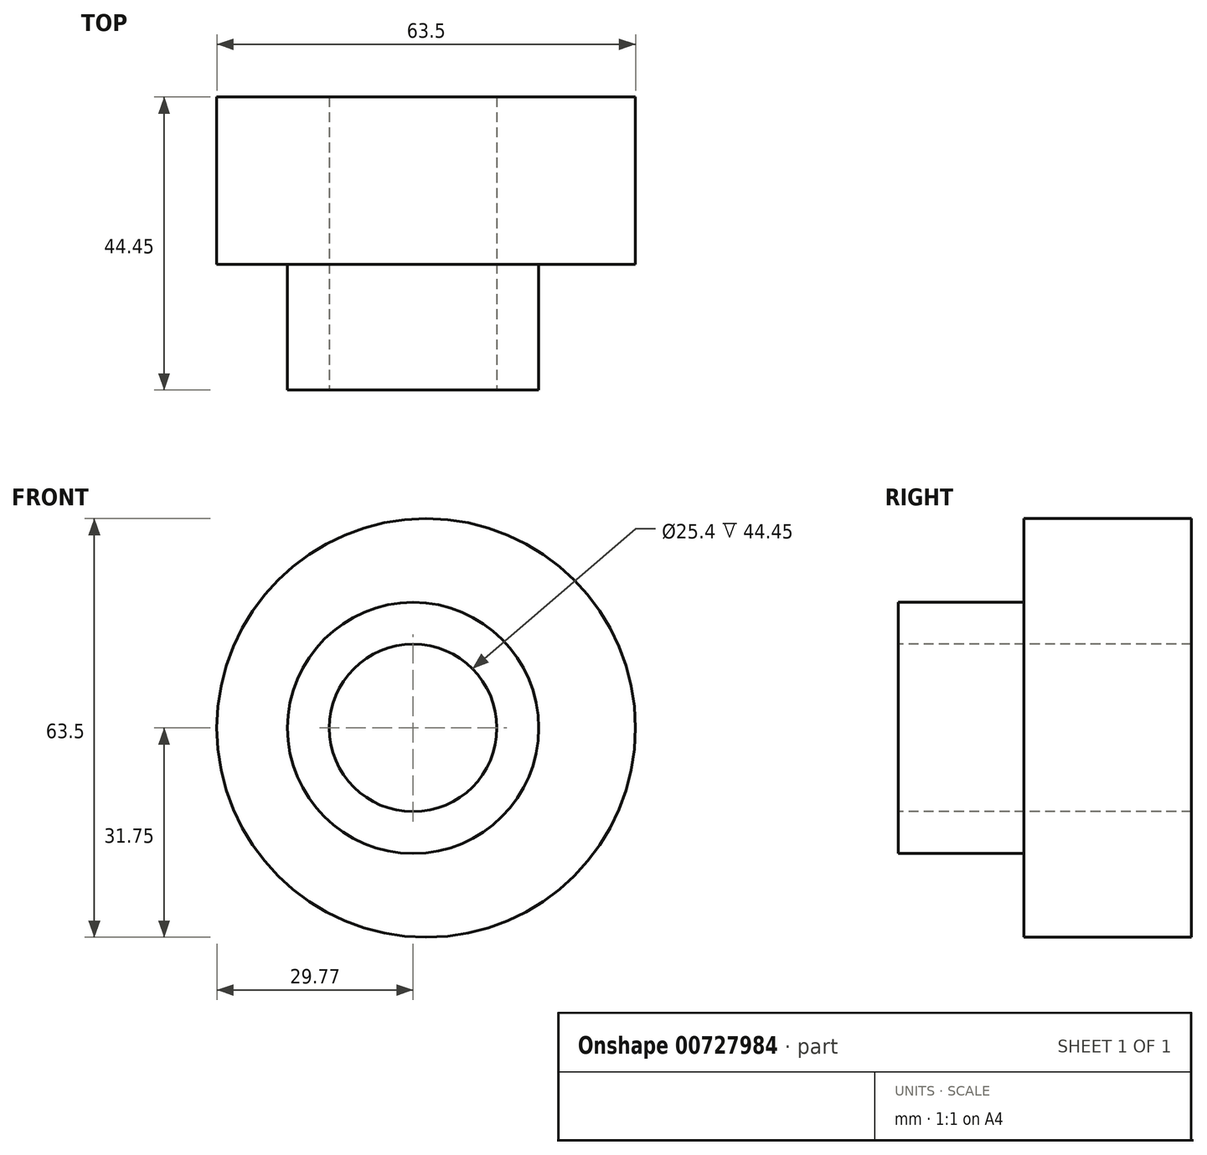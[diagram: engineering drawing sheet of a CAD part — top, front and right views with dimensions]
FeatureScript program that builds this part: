
annotation { "Feature Type Name" : "Feature", "Feature Type Description" : "" }
export const myFeature = defineFeature(function(context is Context, id is Id, definition is map)
    precondition{}
    {
        {
            var Q0;
            Q0=qCreatedBy(makeId("Front.planeOp"),FACE);
            var sketch = newSketch(context, id + "F0", { "sketchPlane" : qUnion([Q0])});
            skLineSegment(sketch, "E0.bottom", {"start": v(-53.38, 54.54) * mm, "end": v(55.94, 54.54) * mm});
            skLineSegment(sketch, "E0.top", {"start": v(-53.38, -62.22) * mm, "end": v(55.94, -62.22) * mm});
            skLineSegment(sketch, "E0.left", {"start": v(-53.38, 54.54) * mm, "end": v(-53.38, -62.22) * mm});
            skLineSegment(sketch, "E0.right", {"start": v(55.94, 54.54) * mm, "end": v(55.94, -62.22) * mm});
            skCircle(sketch, "E1", {"center": v(1.98, 0) * mm, "radius": 31.75 * mm});
            skSolve(sketch);
        }
        {
            var Q0;
            Q0=makeQuery(id+"F0.imprint","IMPRINT",FACE,{"disambiguationData":[TD([[makeQuery(id+"F0.imprint","IMPRINT",EDGE,{"derivedFrom":sQuery(id+"F0.wireOp",EDGE,"E1")}),1.0]])]});
            extrude(context, id + "F1", {"entities" : qUnion([Q0]), "depth" : 25.4 * mm, "offsetDistance" : 25.4 * mm});
        }
        {
            var Q0;
            Q0=makeQuery(id+"F1.opExtrude","CAP_FACE",FACE,{"disambiguationData":[OSD([sQuery(id+"F0.wireOp",EDGE,"E1")])],"isStart":false});
            var sketch = newSketch(context, id + "F2", { "sketchPlane" : qUnion([Q0])});
            skCircle(sketch, "E2", {"center": v(0, 0) * mm, "radius": 19.05 * mm});
            skSolve(sketch);
        }
        {
            var Q0;
            Q0=makeQuery(id+"F2.imprint","IMPRINT",FACE,{"disambiguationData":[TD([[makeQuery(id+"F2.imprint","IMPRINT",EDGE,{"derivedFrom":sQuery(id+"F2.wireOp",EDGE,"E2")}),1.0]])]});
            extrude(context, id + "F3", {"entities" : qUnion([Q0]), "operationType" : NewBodyOperationType.ADD, "depth" : 19.05 * mm, "offsetDistance" : 25.4 * mm});
        }
        {
            var Q0;
            Q0=makeQuery(id+"F3.opExtrude","CAP_FACE",FACE,{"disambiguationData":[OSD([sQuery(id+"F2.wireOp",EDGE,"E2")])],"isStart":false});
            var sketch = newSketch(context, id + "F4", { "sketchPlane" : qUnion([Q0])});
            skCircle(sketch, "E3", {"center": v(0, 0) * mm, "radius": 12.7 * mm});
            skSolve(sketch);
        }
        {
            var Q0;
            Q0 = qSketchRegion(id + "F4", true);
            extrude(context, id + "F5", {"entities" : qUnion([Q0]), "operationType" : NewBodyOperationType.REMOVE, "oppositeDirection" : true, "depth" : 177.8 * mm, "offsetDistance" : 25.4 * mm});
        }
    });
